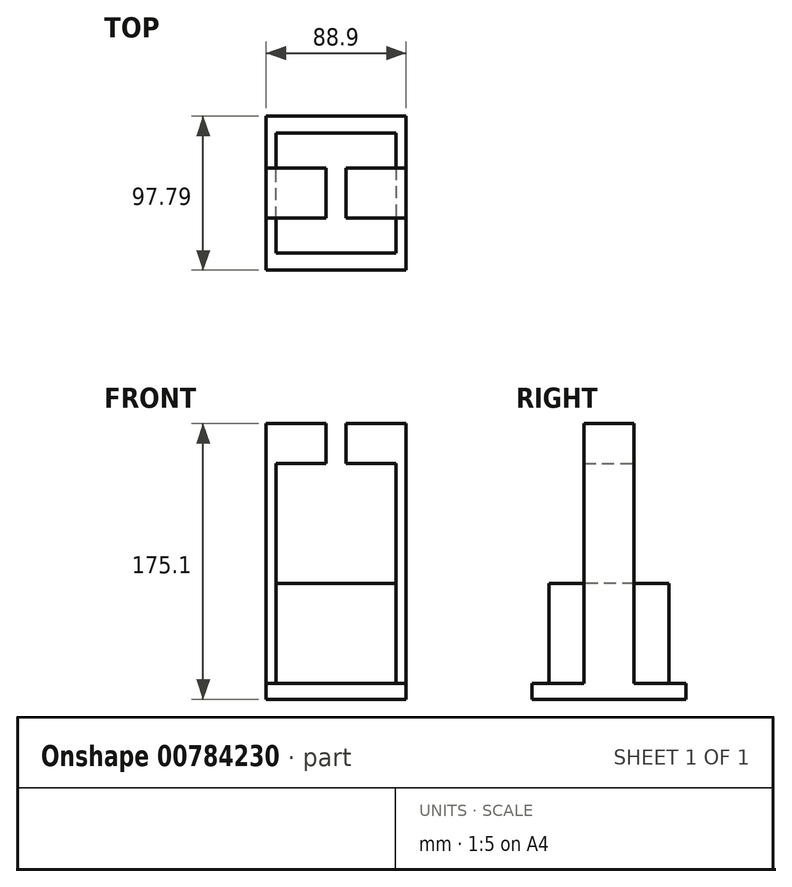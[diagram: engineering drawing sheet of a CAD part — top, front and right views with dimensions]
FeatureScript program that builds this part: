
annotation { "Feature Type Name" : "Feature", "Feature Type Description" : "" }
export const myFeature = defineFeature(function(context is Context, id is Id, definition is map)
    precondition{}
    {
        {
            var Q0;
            Q0=qCreatedBy(makeId("Top.planeOp"),FACE);
            var sketch = newSketch(context, id + "F0", { "sketchPlane" : qUnion([Q0])});
            skLineSegment(sketch, "E0.bottom", {"start": v(-42.5, 79.33) * mm, "end": v(46.4, 79.33) * mm});
            skLineSegment(sketch, "E0.top", {"start": v(-42.5, -18.46) * mm, "end": v(46.4, -18.46) * mm});
            skLineSegment(sketch, "E0.left", {"start": v(-42.5, 79.33) * mm, "end": v(-42.5, -18.46) * mm});
            skLineSegment(sketch, "E0.right", {"start": v(46.4, 79.33) * mm, "end": v(46.4, -18.46) * mm});
            skSolve(sketch);
        }
        {
            var Q0;
            Q0=makeQuery(id+"F0.imprint","IMPRINT",FACE,{"disambiguationData":[TD([[makeQuery(id+"F0.imprint","IMPRINT",EDGE,{"derivedFrom":sQuery(id+"F0.wireOp",EDGE,"E0.bottom")}),-1.0]])]});
            extrude(context, id + "F1", {"entities" : qUnion([Q0]), "depth" : 10 * mm, "offsetDistance" : 25.4 * mm});
        }
        {
            var Q0;
            Q0=makeQuery(id+"F1.opExtrude","CAP_FACE",FACE,{"disambiguationData":[OSD([sQuery(id+"F0.wireOp",EDGE,"E0.bottom"),sQuery(id+"F0.wireOp",EDGE,"E0.top"),sQuery(id+"F0.wireOp",EDGE,"E0.left"),sQuery(id+"F0.wireOp",EDGE,"E0.right")])],"isStart":false});
            var sketch = newSketch(context, id + "F2", { "sketchPlane" : qUnion([Q0])});
            skLineSegment(sketch, "E1.bottom", {"start": v(-36.16, 68.53) * mm, "end": v(40.04, 68.53) * mm});
            skLineSegment(sketch, "E1.top", {"start": v(-36.16, -7.67) * mm, "end": v(40.04, -7.67) * mm});
            skLineSegment(sketch, "E1.left", {"start": v(-36.16, 68.53) * mm, "end": v(-36.16, -7.67) * mm});
            skLineSegment(sketch, "E1.right", {"start": v(40.04, 68.53) * mm, "end": v(40.04, -7.67) * mm});
            skSolve(sketch);
        }
        {
            var Q0;
            Q0=makeQuery(id+"F2.imprint","IMPRINT",FACE,{"disambiguationData":[TD([[makeQuery(id+"F2.imprint","IMPRINT",EDGE,{"derivedFrom":sQuery(id+"F2.wireOp",EDGE,"E1.bottom")}),-1.0]])]});
            extrude(context, id + "F3", {"entities" : qUnion([Q0]), "operationType" : NewBodyOperationType.ADD, "depth" : 63.5 * mm, "offsetDistance" : 25.4 * mm});
        }
        {
            var Q0;
            Q0=makeQuery(id+"F3.opExtrude","SWEPT_FACE",FACE,{"disambiguationData":[OSD([sQuery(id+"F2.wireOp",EDGE,"E1.right")])]});
            var sketch = newSketch(context, id + "F4", { "sketchPlane" : qUnion([Q0])});
            skLineSegment(sketch, "E2.bottom", {"start": v(14.56, 10) * mm, "end": v(46.3, 10) * mm});
            skLineSegment(sketch, "E2.top", {"start": v(14.56, 175.1) * mm, "end": v(46.3, 175.1) * mm});
            skLineSegment(sketch, "E2.left", {"start": v(14.56, 10) * mm, "end": v(14.56, 175.1) * mm});
            skLineSegment(sketch, "E2.right", {"start": v(46.3, 10) * mm, "end": v(46.3, 175.1) * mm});
            skSolve(sketch);
        }
        {
            var Q0;
            Q0 = qSketchRegion(id + "F4", true);
            extrude(context, id + "F5", {"entities" : qUnion([Q0]), "operationType" : NewBodyOperationType.ADD, "depth" : 6.35 * mm, "offsetDistance" : 25.4 * mm});
        }
        {
            var Q0;
            Q0=makeQuery(id+"F3.opExtrude","SWEPT_FACE",FACE,{"disambiguationData":[OSD([sQuery(id+"F2.wireOp",EDGE,"E1.left")])]});
            var sketch = newSketch(context, id + "F6", { "sketchPlane" : qUnion([Q0])});
            skLineSegment(sketch, "E3.bottom", {"start": v(-46.3, 10) * mm, "end": v(-14.56, 10) * mm});
            skLineSegment(sketch, "E3.top", {"start": v(-46.3, 175.1) * mm, "end": v(-14.56, 175.1) * mm});
            skLineSegment(sketch, "E3.left", {"start": v(-46.3, 10) * mm, "end": v(-46.3, 175.1) * mm});
            skLineSegment(sketch, "E3.right", {"start": v(-14.56, 10) * mm, "end": v(-14.56, 175.1) * mm});
            skSolve(sketch);
        }
        {
            var Q0;
            {var subQ0=sQuery(id+"F6.wireOp",EDGE,"E3.top");Q0=makeQuery(id+"F6.imprint","IMPRINT",FACE,{"disambiguationData":[TD([[makeQuery(id+"F6.imprint","IMPRINT",EDGE,{"derivedFrom":subQ0}),-1.0]])]});}
            var Q1;
            {var subQ0=sQuery(id+"F6.wireOp",EDGE,"E3.bottom");Q1=makeQuery(id+"F6.imprint","IMPRINT",FACE,{"disambiguationData":[TD([[makeQuery(id+"F6.imprint","IMPRINT",EDGE,{"derivedFrom":subQ0}),1.0]])]});}
            extrude(context, id + "F7", {"entities" : qUnion([Q0, Q1]), "operationType" : NewBodyOperationType.ADD, "depth" : 6.35 * mm, "offsetDistance" : 25.4 * mm});
        }
        {
            var Q0;
            Q0=makeQuery(id+"F5.opExtrude","CAP_FACE",FACE,{"disambiguationData":[OSD([sQuery(id+"F4.wireOp",EDGE,"E2.bottom"),sQuery(id+"F4.wireOp",EDGE,"E2.top"),sQuery(id+"F4.wireOp",EDGE,"E2.left"),sQuery(id+"F4.wireOp",EDGE,"E2.right")])],"isStart":true});
            var sketch = newSketch(context, id + "F8", { "sketchPlane" : qUnion([Q0])});
            skLineSegment(sketch, "E4.bottom", {"start": v(-46.3, 175.1) * mm, "end": v(-14.56, 175.1) * mm});
            skLineSegment(sketch, "E4.top", {"start": v(-46.3, 149.7) * mm, "end": v(-14.56, 149.7) * mm});
            skLineSegment(sketch, "E4.left", {"start": v(-46.3, 175.1) * mm, "end": v(-46.3, 149.7) * mm});
            skLineSegment(sketch, "E4.right", {"start": v(-14.56, 175.1) * mm, "end": v(-14.56, 149.7) * mm});
            skSolve(sketch);
        }
        {
            var Q0;
            Q0=makeQuery(id+"F8.imprint","IMPRINT",FACE,{"disambiguationData":[TD([[makeQuery(id+"F8.imprint","IMPRINT",EDGE,{"derivedFrom":sQuery(id+"F8.wireOp",EDGE,"E4.bottom")}),1.0]])]});
            extrude(context, id + "F9", {"entities" : qUnion([Q0]), "operationType" : NewBodyOperationType.ADD, "depth" : 31.75 * mm, "offsetDistance" : 25.4 * mm});
        }
        {
            var Q0;
            Q0=makeQuery(id+"F7.opExtrude","CAP_FACE",FACE,{"disambiguationData":[OSD([sQuery(id+"F6.wireOp",EDGE,"E3.bottom"),sQuery(id+"F6.wireOp",EDGE,"E3.top"),sQuery(id+"F6.wireOp",EDGE,"E3.left"),sQuery(id+"F6.wireOp",EDGE,"E3.right")])],"isStart":true});
            var sketch = newSketch(context, id + "F10", { "sketchPlane" : qUnion([Q0])});
            skLineSegment(sketch, "E5.bottom", {"start": v(14.56, 175.1) * mm, "end": v(46.3, 175.1) * mm});
            skLineSegment(sketch, "E5.top", {"start": v(14.56, 149.7) * mm, "end": v(46.3, 149.7) * mm});
            skLineSegment(sketch, "E5.left", {"start": v(14.56, 175.1) * mm, "end": v(14.56, 149.7) * mm});
            skLineSegment(sketch, "E5.right", {"start": v(46.3, 175.1) * mm, "end": v(46.3, 149.7) * mm});
            skSolve(sketch);
        }
        {
            var Q0;
            Q0=makeQuery(id+"F10.imprint","IMPRINT",FACE,{"disambiguationData":[TD([[makeQuery(id+"F10.imprint","IMPRINT",EDGE,{"derivedFrom":sQuery(id+"F10.wireOp",EDGE,"E5.bottom")}),1.0]])]});
            extrude(context, id + "F11", {"entities" : qUnion([Q0]), "operationType" : NewBodyOperationType.ADD, "depth" : 31.75 * mm, "offsetDistance" : 25.4 * mm});
        }
    });
